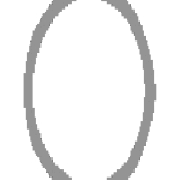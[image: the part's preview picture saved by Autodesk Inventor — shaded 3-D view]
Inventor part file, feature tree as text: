
AUTODESK INVENTOR PART (.ipt)
format: ipt  version: 2021 (Build 250183000, 183)  size: 117,760 bytes
history: native  units: in
note: dims shown in document units (in); Inventor stores cm internally (conversion verified against a paired STEP export)
features: other x4, sketch x3, plane x1
ambient origin geometry x8: Origin, YZ Plane, XZ Plane, XY Plane, X Axis, Y Axis, Z Axis, Center Point
bodies: Solid1 (feature_tree), Body (feature_tree)
feature tree (8):
  other  "Driven Length"
  other  "Frame Generator"
  other  "Start Plane"
  other  "End Plane"
  sketch  "Sketch"  dims[d2=1.5435in d4=-0.0in d5=1.5435in d6=0.12in d7=0.0in d8=90.0deg d9=1.5435in]
  sketch  "Sketch2"  dims[d0=1.0in]
  plane  "Work Plane3"
  sketch  "Sketch3"  dims[d1=0.065in]
